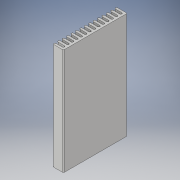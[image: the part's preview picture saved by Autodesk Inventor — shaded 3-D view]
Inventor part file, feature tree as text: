
AUTODESK INVENTOR PART (.ipt)
format: ipt  version: 2019 (Build 230136000, 136)  size: 247,808 bytes
history: native  units: mm
features: fillet x7, extrude x2, sketch x2, other x1, pattern_linear x1
ambient origin geometry x8: Origin, YZ Plane, XZ Plane, XY Plane, X Axis, Y Axis, Z Axis, Center Point
bodies: Body1 (feature_tree)
feature tree (13):
  other  "Bryła1"
  extrude  "Wyciągnięcie proste1"  Depth=10.0mm
  extrude  "Wyciągnięcie proste2"  Depth=5.0mm
  pattern_linear  "Szyk prostokątny1"  Count1=6  [1 undecoded]
  fillet  "Zaokrąglenie1"  Radius=30.0mm
  fillet  "Zaokrąglenie2"  Radius=100.0mm
  fillet  "Zaokrąglenie3"  Radius=2.0mm
  fillet  "Zaokrąglenie4"  Radius=2.0mm
  fillet  "Zaokrąglenie5"  Radius=2.0mm
  fillet  "Zaokrąglenie6"  Radius=100.0mm
  fillet  "Zaokrąglenie7"  Radius=4.15mm
  sketch  "Szkic1"
  sketch  "Szkic2"
note: 1 required parameter value undecoded (feature->parameter linkage not recoverable at this tier; creation-order binding heuristic only, values carry confidence <= 0.55)
